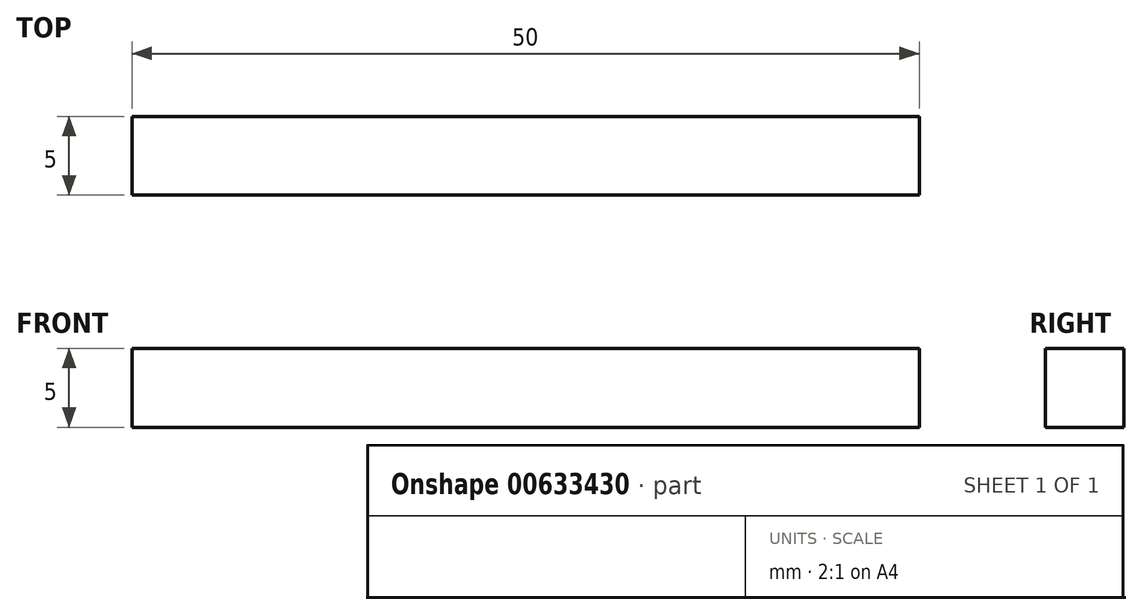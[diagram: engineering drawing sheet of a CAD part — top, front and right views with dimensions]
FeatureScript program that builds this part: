
annotation { "Feature Type Name" : "Feature", "Feature Type Description" : "" }
export const myFeature = defineFeature(function(context is Context, id is Id, definition is map)
    precondition{}
    {
        {
            var Q0;
            Q0=qCreatedBy(makeId("Top.planeOp"),FACE);
            var sketch = newSketch(context, id + "F0", { "sketchPlane" : qUnion([Q0])});
            skLineSegment(sketch, "E0.bottom", {"start": v(0, 0) * mm, "end": v(50, 0) * mm});
            skLineSegment(sketch, "E0.top", {"start": v(0, 5) * mm, "end": v(50, 5) * mm});
            skLineSegment(sketch, "E0.left", {"start": v(0, 0) * mm, "end": v(0, 5) * mm});
            skLineSegment(sketch, "E0.right", {"start": v(50, 0) * mm, "end": v(50, 5) * mm});
            skSolve(sketch);
        }
        {
            var Q0;
            Q0 = qSketchRegion(id + "F0", true);
            extrude(context, id + "F1", {"entities" : qUnion([Q0]), "depth" : 5 * mm, "offsetDistance" : 25 * mm});
        }
    });
